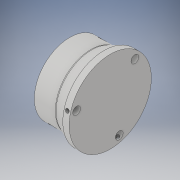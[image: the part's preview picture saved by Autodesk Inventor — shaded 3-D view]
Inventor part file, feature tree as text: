
AUTODESK INVENTOR PART (.ipt)
format: ipt  version: 2019 (Build 230136000, 136)  size: 335,872 bytes
history: native  units: in
note: dims shown in document units (in); Inventor stores cm internally (conversion verified against a paired STEP export)
features: sketch x16, extrude x11, plane x4, pattern_circular x2, mirror x2, thread x2, fillet x2, projected_geometry x2, revolve x1
ambient origin geometry x8: Origin, YZ Plane, XZ Plane, XY Plane, X Axis, Y Axis, Z Axis, Center Point
bodies: Solid1 (feature_tree), Solid2 (feature_tree)
feature tree (42):
  extrude  "Extrusion1"  Depth=1.7323in
  extrude  "Extrusion3"  Depth=1.2402in
  extrude  "Extrusion4"  Depth=1.1811in TaperAngle=0.0deg
  pattern_circular  "Circular Pattern1"  Count=4 Angle=360.0deg
  sketch  "Sketch6"  dims[d16=0.3937in d17=45.0deg]
  plane  "Work Plane1"
  extrude  "Extrusion5"  TaperAngle=45.0deg  [1 undecoded]
  plane  "Work Plane2"
  mirror  "Mirror1"
  extrude  "Extrusion6"  TaperAngle=45.0deg  [1 undecoded]
  extrude  "Extrusion7"  Depth=0.2362in TaperAngle=0.0deg
  sketch  "Sketch11"  dims[d26=0.3937in d27=0.0in d28=0.0118in]
  plane  "Work Plane3"
  extrude  "Extrusion8"  TaperAngle=45.0deg  [1 undecoded]
  thread  "Thread1"  [1 undecoded]
  mirror  "Mirror2"
  extrude  "Extrusion9"  Depth=0.3937in
  revolve  "Revolution1"  [1 undecoded]
  fillet  "Fillet1"  Radius=0.4724in
  fillet  "Fillet2"  Radius=0.0098in
  extrude  "Extrusion10"  Depth=0.4724in
  extrude  "Extrusion11"  Depth=0.3937in TaperAngle=0.0deg
  sketch  "Sketch18"  dims[d46=1.2795in]
  plane  "Work Plane4"
  sketch  "Sketch19"  dims[d47=90.0deg]
  extrude  "Extrusion12"  Depth=0.3937in TaperAngle=0.0deg
  thread  "Thread2"  [1 undecoded]
  pattern_circular  "Circular Pattern2"  [2 undecoded]
  sketch  "Sketch2"  dims[d3=0.7874in d4=1.7323in]
  sketch  "Sketch4"  dims[d5=0.4724in d6=0.0in d9=1.2402in]
  sketch  "Sketch5"  dims[d10=0.2008in d11=1.1811in d12=0.0in d13=1.5748in d14=360.0deg]
  sketch  "Sketch7"  dims[d18=0.1181in d19=45.0deg]
  sketch  "Sketch8"  dims[d20=0.3543in d21=0.2362in d22=0.0in]
  projected_geometry  "Projected Loop1"
  sketch  "Sketch9"  dims[d23=0.8661in d24=45.0deg d25=0.2047in]
  sketch  "Sketch12"  dims[d29=0.4724in d30=0.0in d31=0.2362in d32=0.4724in d33=0.0in d34=0.0098in]
  sketch  "Sketch13"  dims[d35=45.0deg d36=0.4724in]
  sketch  "Sketch14"  dims[d37=0.1969in d38=0.3937in d39=0.0in]
  sketch  "Sketch15"  dims[d40=0.3937in d41=0.0in d42=0.1969in d43=0.0in d44=0.3937in]
  projected_geometry  "Projected Loop2"
  sketch  "Sketch17"  dims[d45=180.0deg]
  sketch  "Sketch20"  dims[d48=90.0deg d49=0.0787in d50=0.0157in d51=0.1969in d52=0.0in d53=1.0827in d54=45.0deg d55=0.2402in d56=0.1969in d57=0.0in d58=45.0deg d59=0.1969in d60=180.0deg d61=0.1181in d62=0.1181in d63=0.0in d64=1.1811in d65=360.0deg d67=0.3937in d68=0.0in]
note: 8 required parameter values undecoded (feature->parameter linkage not recoverable at this tier; creation-order binding heuristic only, values carry confidence <= 0.55)